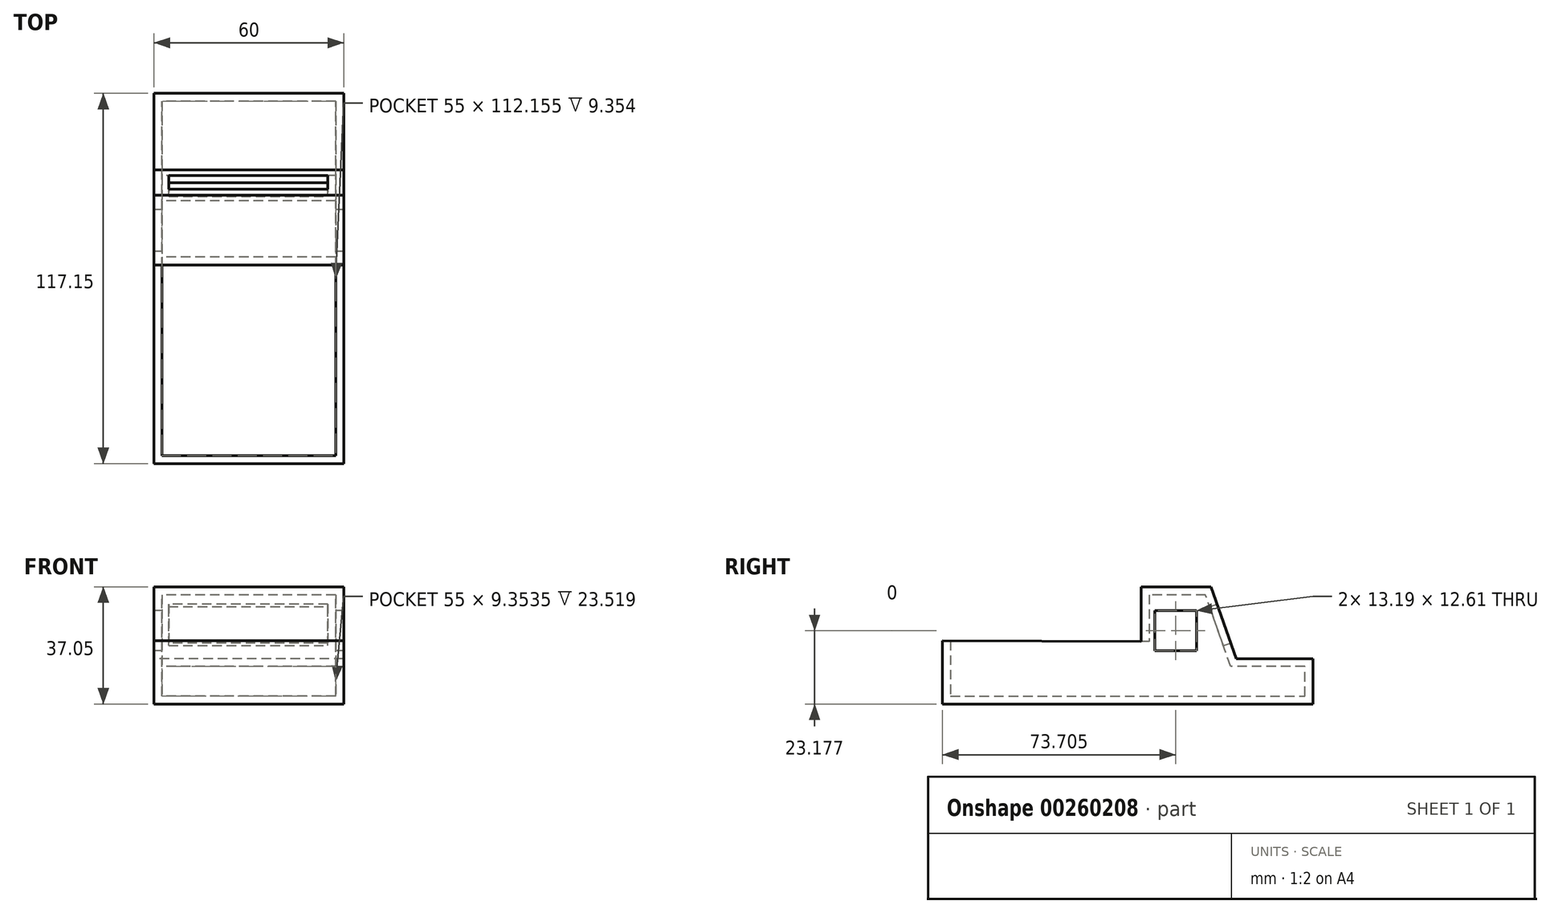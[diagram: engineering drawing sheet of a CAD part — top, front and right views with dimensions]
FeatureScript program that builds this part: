
annotation { "Feature Type Name" : "Feature", "Feature Type Description" : "" }
export const myFeature = defineFeature(function(context is Context, id is Id, definition is map)
    precondition{}
    {
        {
            var Q0;
            Q0=qCreatedBy(makeId("Right.planeOp"),FACE);
            var sketch = newSketch(context, id + "F0", { "sketchPlane" : qUnion([Q0])});
            skLineSegment(sketch, "E0", {"start": v(-67.11, 9.12) * mm, "end": v(-67.11, -10.86) * mm});
            skLineSegment(sketch, "E1", {"start": v(-67.11, -10.86) * mm, "end": v(50.04, -10.86) * mm});
            skLineSegment(sketch, "E2", {"start": v(50.04, -10.86) * mm, "end": v(50.04, 3.5) * mm});
            skLineSegment(sketch, "E3", {"start": v(50.04, 3.5) * mm, "end": v(25.8, 3.5) * mm});
            skLineSegment(sketch, "E4", {"start": v(25.8, 3.5) * mm, "end": v(17.84, 26.19) * mm});
            skLineSegment(sketch, "E5", {"start": v(17.84, 26.19) * mm, "end": v(-4.27, 26.19) * mm});
            skLineSegment(sketch, "E6", {"start": v(-4.27, 26.19) * mm, "end": v(-4.27, 8.92) * mm});
            skLineSegment(sketch, "E7", {"start": v(-4.27, 8.92) * mm, "end": v(-67.11, 9.12) * mm});
            skSolve(sketch);
        }
        {
            var Q0;
            Q0 = qSketchRegion(id + "F0", true);
            extrude(context, id + "F1", {"entities" : qUnion([Q0]), "depth" : 60 * mm});
        }
        {
            var Q0;
            Q0=makeQuery(id+"F1.opExtrude","SWEPT_FACE",FACE,{"disambiguationData":[OSD([sQuery(id+"F0.wireOp",EDGE,"E7")])]});
            shell(context, id + "F2", {"entities" : qUnion([Q0]), "thickness" : 2.5 * mm});
        }
        {
            var Q0;
            Q0=qCreatedBy(makeId("Right.planeOp"),FACE);
            var sketch = newSketch(context, id + "F3", { "sketchPlane" : qUnion([Q0])});
            skCircle(sketch, "E8", {"center": v(31.62, -10.67) * mm, "radius": 11.3 * mm});
            skCircle(sketch, "E9", {"center": v(-56.06, -10.86) * mm, "radius": 10.09 * mm});
            skLineSegment(sketch, "E10.bottom", {"start": v(13.19, 18.62) * mm, "end": v(0, 18.62) * mm});
            skLineSegment(sketch, "E10.top", {"start": v(13.19, 6.01) * mm, "end": v(0, 6.01) * mm});
            skLineSegment(sketch, "E10.left", {"start": v(13.19, 18.62) * mm, "end": v(13.19, 6.01) * mm});
            skLineSegment(sketch, "E10.right", {"start": v(0, 18.62) * mm, "end": v(0, 6.01) * mm});
            skSolve(sketch);
        }
        {
            var Q0;
            Q0=makeQuery(id+"F3.imprint","IMPRINT",FACE,{"disambiguationData":[TD([[makeQuery(id+"F3.imprint","IMPRINT",EDGE,{"derivedFrom":sQuery(id+"F3.wireOp",EDGE,"E10.bottom")}),1.0]])]});
            extrude(context, id + "F4", {"entities" : qUnion([Q0]), "operationType" : NewBodyOperationType.REMOVE, "depth" : 60 * mm});
        }
        {
            var Q0;
            Q0=makeQuery(id+"F1.opExtrude","SWEPT_FACE",FACE,{"disambiguationData":[OSD([sQuery(id+"F0.wireOp",EDGE,"E4")])]});
            var sketch = newSketch(context, id + "F5", { "sketchPlane" : qUnion([Q0])});
            skLineSegment(sketch, "E11.bottom", {"start": v(-54.99, 13.02) * mm, "end": v(-4.6, 13.02) * mm});
            skLineSegment(sketch, "E11.top", {"start": v(-54.99, 0) * mm, "end": v(-4.6, 0) * mm});
            skLineSegment(sketch, "E11.left", {"start": v(-54.99, 13.02) * mm, "end": v(-54.99, 0) * mm});
            skLineSegment(sketch, "E11.right", {"start": v(-4.6, 13.02) * mm, "end": v(-4.6, 0) * mm});
            skSolve(sketch);
        }
        {
            var Q0;
            Q0=makeQuery(id+"F5.imprint","IMPRINT",FACE,{"disambiguationData":[TD([[makeQuery(id+"F5.imprint","IMPRINT",EDGE,{"derivedFrom":sQuery(id+"F5.wireOp",EDGE,"E11.bottom")}),-1.0]])]});
            extrude(context, id + "F6", {"entities" : qUnion([Q0]), "operationType" : NewBodyOperationType.REMOVE, "oppositeDirection" : true, "depth" : 15.4 * mm, "offsetDistance" : 25 * mm});
        }
    });
